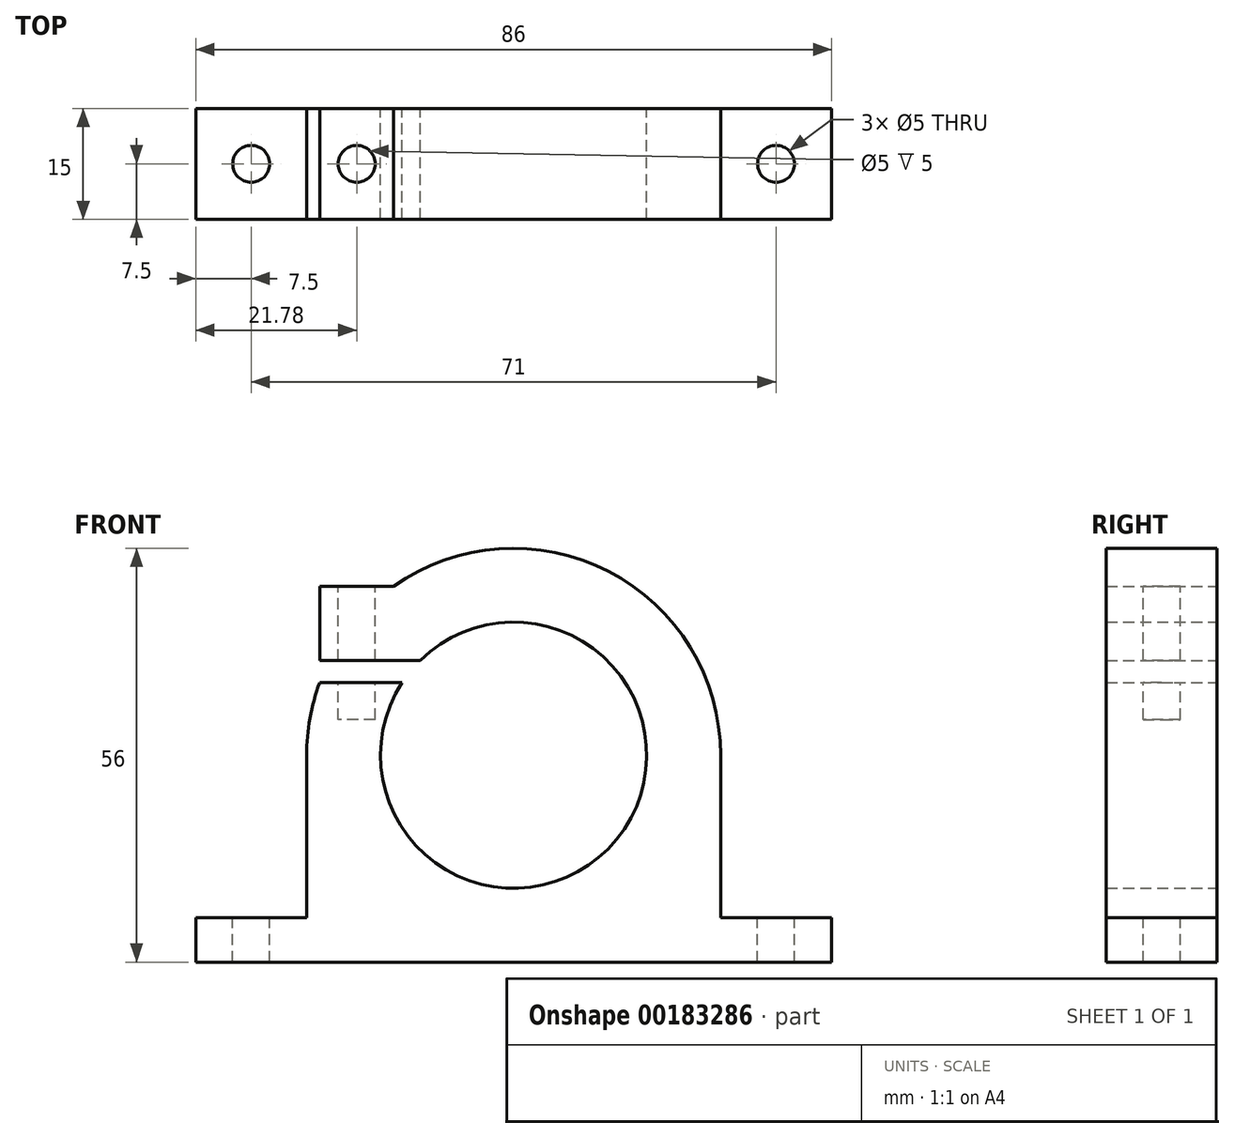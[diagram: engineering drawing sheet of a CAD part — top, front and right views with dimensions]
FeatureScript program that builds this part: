
annotation { "Feature Type Name" : "Feature", "Feature Type Description" : "" }
export const myFeature = defineFeature(function(context is Context, id is Id, definition is map)
    precondition{}
    {
        {
            var Q0;
            Q0=qCreatedBy(makeId("Front.planeOp"),FACE);
            var sketch = newSketch(context, id + "F0", { "sketchPlane" : qUnion([Q0])});
            skArc(sketch, "E0", {"start": v(-16.22, 22.82) * mm, "mid": v(12.84, 24.88) * mm, "end": v(28, 0) * mm});
            skArc(sketch, "E1", {"start": v(-15.08, 9.82) * mm, "mid": v(13.94, -11.39) * mm, "end": v(-12.63, 12.82) * mm});
            skLineSegment(sketch, "E2", {"start": v(-15.08, 9.82) * mm, "end": v(-26.22, 9.82) * mm});
            skLineSegment(sketch, "E3", {"start": v(-16.22, 22.82) * mm, "end": v(-26.22, 22.82) * mm});
            skLineSegment(sketch, "E4", {"start": v(-26.22, 22.82) * mm, "end": v(-26.22, 12.82) * mm});
            skLineSegment(sketch, "E5", {"start": v(-26.22, 12.82) * mm, "end": v(-12.63, 12.82) * mm});
            skLineSegment(sketch, "E6", {"start": v(0, 18) * mm, "end": v(0, 28) * mm, "construction": true});
            skLineSegment(sketch, "E7", {"start": v(-43, -28) * mm, "end": v(43, -28) * mm});
            skPoint(sketch, "E8", {"position": v(0, -28) * mm});
            skLineSegment(sketch, "E9", {"start": v(-43, -28) * mm, "end": v(-43, -22) * mm});
            skLineSegment(sketch, "E10", {"start": v(-43, -22) * mm, "end": v(-28, -22) * mm});
            skLineSegment(sketch, "E11", {"start": v(-28, -22) * mm, "end": v(-28, 0) * mm});
            skLineSegment(sketch, "E12.MirrorCS", {"start": v(43, -28) * mm, "end": v(43, -22) * mm});
            skLineSegment(sketch, "E13.MirrorCS", {"start": v(43, -22) * mm, "end": v(28, -22) * mm});
            skLineSegment(sketch, "E14.MirrorCS", {"start": v(28, -22) * mm, "end": v(28, 0) * mm});
            skArc(sketch, "E15", {"start": v(-28, 0) * mm, "mid": v(-27.55, 5) * mm, "end": v(-26.22, 9.82) * mm});
            skArc(sketch, "E16", {"start": v(28, 0) * mm, "mid": v(0, -28) * mm, "end": v(-28, 0) * mm, "construction": true});
            skSolve(sketch);
        }
        {
            var Q0;
            Q0 = qSketchRegion(id + "F0", true);
            extrude(context, id + "F1", {"entities" : qUnion([Q0]), "endBound" : BoundingType.SYMMETRIC, "depth" : 15 * mm});
        }
        {
            var Q0;
            Q0=makeQuery(id+"F1.opExtrude","SWEPT_FACE",FACE,{"disambiguationData":[OSD([sQuery(id+"F0.wireOp",EDGE,"E10")])]});
            var sketch = newSketch(context, id + "F2", { "sketchPlane" : qUnion([Q0])});
            skCircle(sketch, "E17", {"center": v(-35.5, 0) * mm, "radius": 2.5 * mm});
            skCircle(sketch, "E18.MirrorC", {"center": v(35.5, 0) * mm, "radius": 2.5 * mm});
            skSolve(sketch);
        }
        {
            var Q0;
            Q0 = qSketchRegion(id + "F2", true);
            extrude(context, id + "F3", {"entities" : qUnion([Q0]), "operationType" : NewBodyOperationType.REMOVE, "endBound" : BoundingType.UP_TO_NEXT, "oppositeDirection" : true, "depth" : 25 * mm});
        }
        {
            var Q0;
            Q0=makeQuery(id+"F1.opExtrude","SWEPT_FACE",FACE,{"disambiguationData":[OSD([sQuery(id+"F0.wireOp",EDGE,"E3")])]});
            var sketch = newSketch(context, id + "F4", { "sketchPlane" : qUnion([Q0])});
            skCircle(sketch, "E19", {"center": v(-21.22, 0) * mm, "radius": 2.5 * mm});
            skSolve(sketch);
        }
        {
            var Q0;
            Q0 = qSketchRegion(id + "F4", true);
            extrude(context, id + "F5", {"entities" : qUnion([Q0]), "operationType" : NewBodyOperationType.REMOVE, "oppositeDirection" : true, "depth" : 18 * mm});
        }
    });
